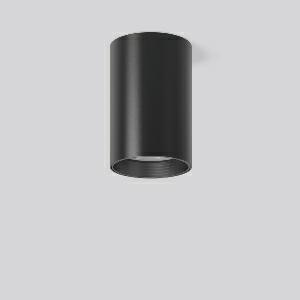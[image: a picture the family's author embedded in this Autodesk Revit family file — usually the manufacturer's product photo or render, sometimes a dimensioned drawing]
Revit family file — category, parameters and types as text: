
# Revit family: heledon_maxi_a_931222_003_2_76_b6c6
name_source: partatom
category: Lighting Fixtures
units: mm (PartAtom-declared; Revit-internal decimal feet)

## family parameters
Cut with Voids When Loaded = No
Host = Face
Light Source = No
Part Type = Normal
Room Calculation Point = No
Round Connector Dimension = Use Diameter
Shared = No

## types (1)
- HELEDON maxi A (1 x LED Modul 927, 2650 lm, 2700)
    Apparent Load = 25 VA
    Approval mark = CE
    CIE Flux Codes = 96 100 100 100 100
    Color Rendering = 92
    Color Temperature = 2700
    Default Elevation = 1800 mm
    Description = Series: HELEDON maxi
Cylindrical surface-mounted downlight. Housing: die-cast aluminium, powder-coated. Internal ceiling frame polycarbonate with bayonet mounting. Black plastic ring and recessed LED to prevent glare from the side. Optical assembly with lens made of plastic (polycarbonate) for the best homogeneous light distribution - can be changed without tools. Best colour rendering index Ra>90. Suitable for Ceiling mounting. Easy installation with a separate ceiling frame with bayonet mounting and plug connection. Driver integrated. Connected via plug-in connector. High quality converter without flickering and stroboscopic effect. The following accessories can be mounted without use of tools: interchangeable lenses, decorative glasses, honeycomb louvre, clear and frosted diffusers, white interchangeable plastic ring. 
Colour: deep black, matt (RAL 9005)
Diameter: 123 mm
Height: 183 mm
Lamp: LED
Socket: without socket
Colour temperature: 2700K
Colour rendering index (CRI): 92
System power: 25 W
Rated luminous flux: 2650 lm
Luminous efficiency: 106 lm/W
Control gear: Converter, dimmable, DALI
Protection class: I
Type of protection: IP 20
    Height = 183 mm
    Lamp = 1 x LED Modul 927
    Lamp Light Flux = 2650 lm
    Lamp count = 1
    Length = 123 mm
    Lifetime = 50000 h
    Luminous efficacy = 106 lm/W
    Manufacturer = RZB
    ModVariant = No
    Model = 931222.003.2.76
    Mounting Place = Ceiling
    Mounting Type = Surface mounted
    Number of Poles = 1
    OnlyDefault = Yes
    Power Factor = 1
    Product Name = HELEDON maxi A
    Product group = Surface mounted downlights
    ProductGroupID = 302
    Protection Class = Protection class I
    Protection Degree = IP 20
    RLX_Detail_Level = 1
    RLX_Emergency_Light_Flux = 0 lm
    RLX_Emergency_Type = 0
    RLX_Emergency_Type_DB = No
    RlxData = <blob elided: 98601 chars, md5=831aba02>
    Socket = socket
    Standby Power = 0 W
    System Light Flux = 2650 lm
    System Power = 25 W
    Type Comments = Product without accessories
    Type Image = 931193.003.jpg
    URL = http://relux.com
    VarID = ---
    Voltage = 230 V
    Voltage Range = 220-240 V
    Weight = 0.00 kg
    Width = 0 mm  [stored 0 ft]

note: [stored X ft] marks values corroborated as IEEE doubles in the binary element streams (Revit-internal decimal feet)

## geometry (parser evidence)
native form markers: Blend x4, Sweep x10
no freeform markers — native parametric forms only
